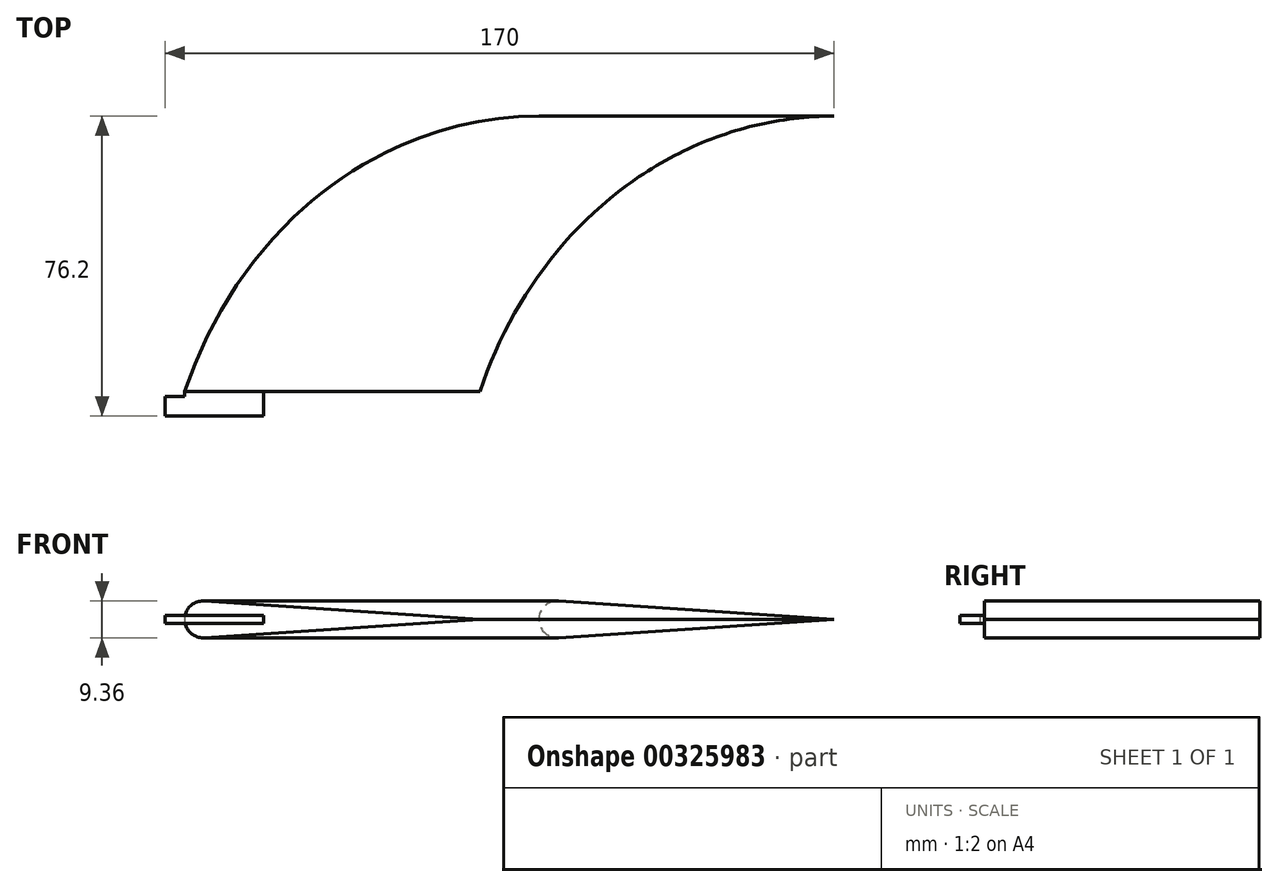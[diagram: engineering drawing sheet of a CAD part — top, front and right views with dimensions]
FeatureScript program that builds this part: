
annotation { "Feature Type Name" : "Feature", "Feature Type Description" : "" }
export const myFeature = defineFeature(function(context is Context, id is Id, definition is map)
    precondition{}
    {
        {
            var Q0;
            Q0=qCreatedBy(makeId("Top.planeOp"),FACE);
            var sketch = newSketch(context, id + "F0", { "sketchPlane" : qUnion([Q0])});
            skLineSegment(sketch, "E0", {"start": v(-75, 0) * mm, "end": v(0, 0) * mm});
            skEllipticalArc(sketch, "E1", {});
            skLineSegment(sketch, "E2", {"start": v(90, -37.61) * mm, "end": v(90, 70) * mm});
            skEllipticalArc(sketch, "E3", {});
            skLineSegment(sketch, "E4", {"start": v(-75, 0) * mm, "end": v(-75, -1.2) * mm});
            skLineSegment(sketch, "E5", {"start": v(-75, -1.2) * mm, "end": v(-80, -1.2) * mm});
            skLineSegment(sketch, "E6", {"start": v(-80, -1.2) * mm, "end": v(-80, -6.2) * mm});
            skLineSegment(sketch, "E7", {"start": v(-80, -6.2) * mm, "end": v(-55, -6.2) * mm});
            skLineSegment(sketch, "E8", {"start": v(-55, -6.2) * mm, "end": v(-55, 0) * mm});
            skLineSegment(sketch, "E9", {"start": v(30.28, 85) * mm, "end": v(-83.36, 85) * mm, "construction": true});
            skLineSegment(sketch, "E10.bottom", {"start": v(-51.5, 0) * mm, "end": v(-16.5, 0) * mm});
            skLineSegment(sketch, "E10.top", {"start": v(-51.5, -6.2) * mm, "end": v(-16.5, -6.2) * mm});
            skLineSegment(sketch, "E10.left", {"start": v(-51.5, 0) * mm, "end": v(-51.5, -6.2) * mm});
            skLineSegment(sketch, "E10.right", {"start": v(-16.5, 0) * mm, "end": v(-16.5, -6.2) * mm});
            const initialGuessF0  = {"E1": [0.09, -0.03761064403689551, 0, -1, 0.10761064403689552, 0.09605800834322765, 3.141592653589793, 4.355344403783013], "E3": [0.030278365384769176, 0, -1, 0, 0.1052783653847692, 0.085, 4.1091975747750205, 0.07300601137536593]};
            skSetInitialGuess(sketch, initialGuessF0);
            skSolve(sketch);
        }
        {
            var Q0;
            {var subQ0=sQuery(id+"F0.wireOp",EDGE,"E0");Q0=makeQuery(id+"F0.imprint","IMPRINT",FACE,{"disambiguationData":[TD([[makeQuery(id+"F0.imprint","IMPRINT",EDGE,{"derivedFrom":subQ0}),1.0]])]});}
            extrude(context, id + "F1", {"entities" : qUnion([Q0]), "depth" : 10 * mm, "offsetDistance" : 25 * mm, "symmetric" : true});
        }
        {
            var Q0;
            Q0=qCreatedBy(makeId("Front.planeOp"),FACE);
            var sketch = newSketch(context, id + "F2", { "sketchPlane" : qUnion([Q0])});
            skLineSegment(sketch, "E11", {"start": v(0, 0) * mm, "end": v(-70.01, -4.67) * mm});
            skPoint(sketch, "E12.0.1.end.orphan", {"position": v(0, 5) * mm});
            skArc(sketch, "E13", {"start": v(-70.01, 4.67) * mm, "mid": v(-75, 0) * mm, "end": v(-70.01, -4.67) * mm});
            skLineSegment(sketch, "E14.trimOffspring", {"start": v(-70.01, 4.67) * mm, "end": v(0, 0) * mm});
            skPoint(sketch, "E15.trimOffspring.end.orphan", {"position": v(-75, -5) * mm});
            skPoint(sketch, "E16.center.orphan", {"position": v(-75, 0) * mm});
            skPoint(sketch, "E16.end.orphan", {"position": v(-75, 5) * mm});
            skLineSegment(sketch, "E17.0", {"start": v(-75, 0) * mm, "end": v(0, 0) * mm});
            skSolve(sketch);
        }
        {
            var Q0;
            Q0 = qSketchRegion(id + "F2", true);
            var Q1;
            Q1=sQuery(id+"F0.wireOp",EDGE,"E1");
            sweep(context, id + "F3", {"operationType" : NewBodyOperationType.INTERSECT, "profiles" : qUnion([Q0]), "path" : qUnion([Q1]), "profileControl" : ProfileControlMode.KEEP_ORIENTATION});
        }
        {
            var Q0;
            {var subQ3=sQuery(id+"F0.wireOp",EDGE,"E8");Q0=makeQuery(id+"F0.imprint","IMPRINT",FACE,{"disambiguationData":[TD([[makeQuery(id+"F0.imprint","IMPRINT",EDGE,{"derivedFrom":subQ3}),1.0]])]});}
            var Q1;
            {var subQ1=sQuery(id+"F0.wireOp",EDGE,"E4");Q1=makeQuery(id+"F0.imprint","IMPRINT",FACE,{"disambiguationData":[TD([[makeQuery(id+"F0.imprint","IMPRINT",EDGE,{"derivedFrom":subQ1}),1.0]])]});}
            var Q2;
            Q2=makeQuery(id+"F0.imprint","IMPRINT",FACE,{"disambiguationData":[TD([[makeQuery(id+"F0.imprint","IMPRINT",EDGE,{"derivedFrom":sQuery(id+"F0.wireOp",EDGE,"E10.bottom")}),-1.0]])]});
            var Q3;
            Q3=makeQuery(id+"F1.opExtrude","CAP_FACE",FACE,{"disambiguationData":[OSD([sQuery(id+"F0.wireOp",EDGE,"E0"),sQuery(id+"F0.wireOp",EDGE,"E1"),sQuery(id+"F0.wireOp",EDGE,"E3")])],"isStart":false});
            extrude(context, id + "F4", {"entities" : qUnion([Q0, Q1, Q2]), "operationType" : NewBodyOperationType.ADD, "depth" : 2 * mm, "endBoundEntityFace" : qUnion([Q3]), "offsetDistance" : 25 * mm, "symmetric" : true});
        }
    });
